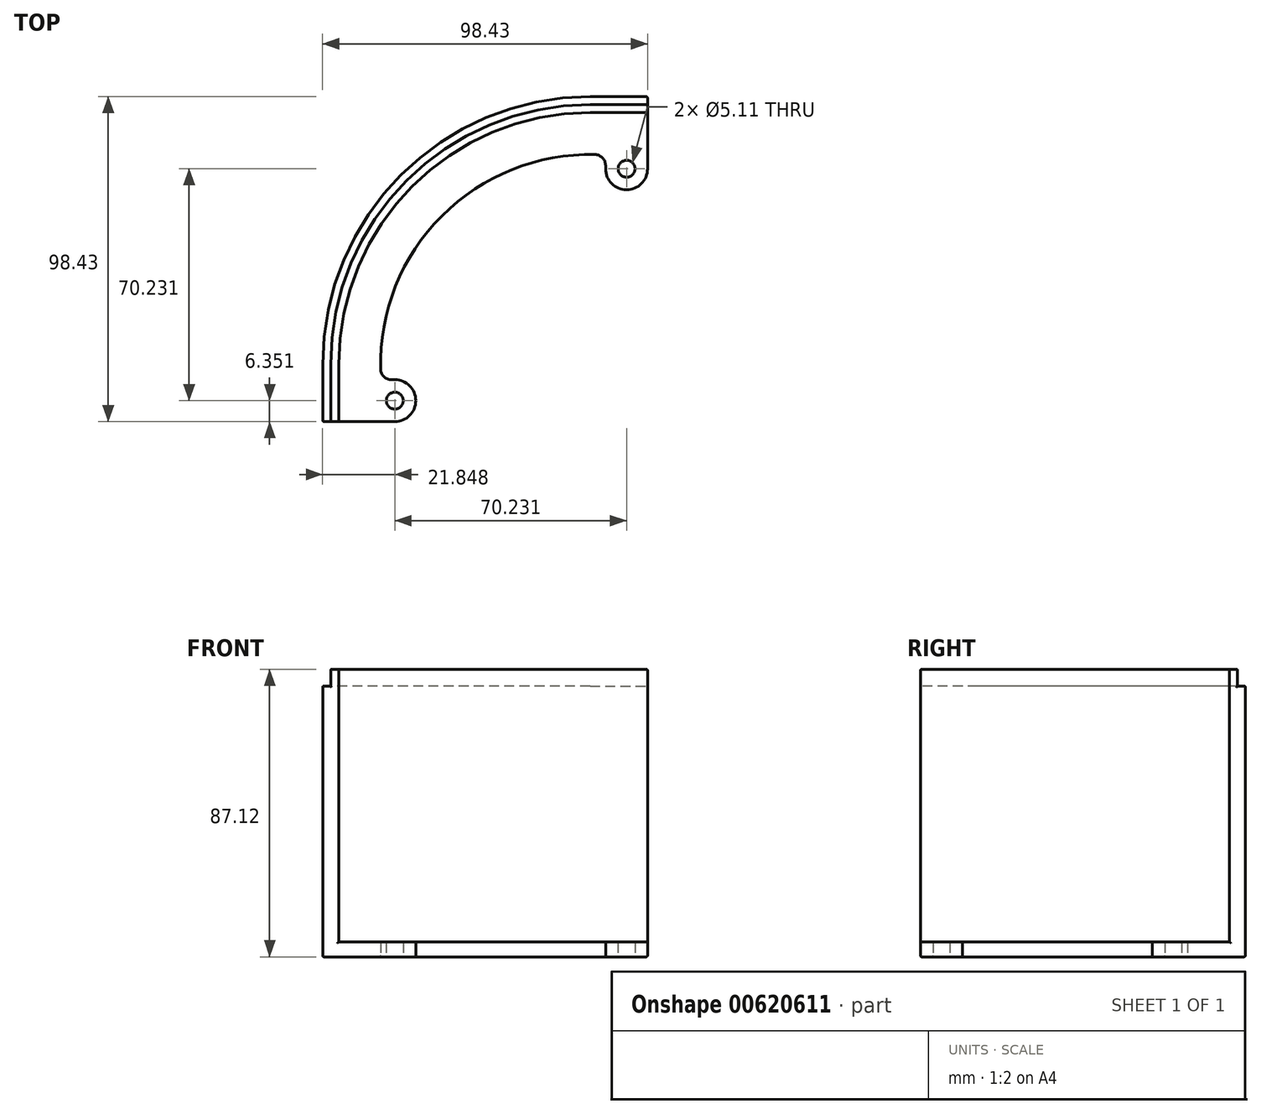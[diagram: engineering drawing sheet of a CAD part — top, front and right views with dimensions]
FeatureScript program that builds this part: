
annotation { "Feature Type Name" : "Feature", "Feature Type Description" : "" }
export const myFeature = defineFeature(function(context is Context, id is Id, definition is map)
    precondition{}
    {
        {
            var Q0;
            Q0=qCreatedBy(makeId("Top.planeOp"),FACE);
            var sketch = newSketch(context, id + "F0", { "sketchPlane" : qUnion([Q0])});
            skArc(sketch, "E0", {"start": v(1.47, 63.48) * mm, "mid": v(-44.9, 44.9) * mm, "end": v(-63.48, -1.47) * mm});
            skArc(sketch, "E1", {"start": v(0, 81.03) * mm, "mid": v(-57.3, 57.3) * mm, "end": v(-81.03, 0) * mm});
            skLineSegment(sketch, "E2", {"start": v(-81.03, 0) * mm, "end": v(-81.03, -17.4) * mm});
            skLineSegment(sketch, "E3", {"start": v(0, 81.03) * mm, "end": v(17.4, 81.03) * mm});
            skLineSegment(sketch, "E4", {"start": v(-81.03, -17.4) * mm, "end": v(-59.18, -17.4) * mm});
            skLineSegment(sketch, "E5", {"start": v(17.4, 81.03) * mm, "end": v(17.4, 59.18) * mm});
            skLineSegment(sketch, "E6", {"start": v(-60.18, -4.7) * mm, "end": v(-59.18, -4.7) * mm});
            skPoint(sketch, "E7.start.orphan", {"position": v(-63.5, 0) * mm});
            skArc(sketch, "E8", {"start": v(-59.18, -17.4) * mm, "mid": v(-52.83, -11.05) * mm, "end": v(-59.18, -4.7) * mm});
            skLineSegment(sketch, "E9.0", {"start": v(4.7, 60.18) * mm, "end": v(4.7, 59.18) * mm});
            skArc(sketch, "E10", {"start": v(4.7, 59.18) * mm, "mid": v(11.05, 52.83) * mm, "end": v(17.4, 59.18) * mm});
            skCircle(sketch, "E11", {"center": v(11.05, 59.18) * mm, "radius": 2.55 * mm});
            skCircle(sketch, "E12", {"center": v(-59.18, -11.05) * mm, "radius": 2.55 * mm});
            skPoint(sketch, "E13.visualSharp", {"position": v(4.7, 63.33) * mm});
            skArc(sketch, "E13.filletArc", {"start": v(4.7, 60.18) * mm, "mid": v(3.76, 62.49) * mm, "end": v(1.47, 63.48) * mm});
            skPoint(sketch, "E14.visualSharp", {"position": v(-63.33, -4.7) * mm});
            skArc(sketch, "E14.filletArc", {"start": v(-63.48, -1.47) * mm, "mid": v(-62.49, -3.76) * mm, "end": v(-60.18, -4.7) * mm});
            skArc(sketch, "E15", {"start": v(0, 78.61) * mm, "mid": v(-55.59, 55.59) * mm, "end": v(-78.61, 0) * mm});
            skLineSegment(sketch, "E16", {"start": v(0, 78.61) * mm, "end": v(17.4, 78.61) * mm});
            skLineSegment(sketch, "E17", {"start": v(-78.61, 0) * mm, "end": v(-78.61, -17.4) * mm});
            skArc(sketch, "E18", {"start": v(0, 76.2) * mm, "mid": v(-53.88, 53.88) * mm, "end": v(-76.2, 0) * mm});
            skLineSegment(sketch, "E19", {"start": v(0, 76.2) * mm, "end": v(17.4, 76.2) * mm});
            skLineSegment(sketch, "E20", {"start": v(-76.2, 0) * mm, "end": v(-76.2, -17.4) * mm});
            skSolve(sketch);
        }
        {
            var Q0;
            Q0=makeQuery(id+"F0.imprint","IMPRINT",FACE,{"disambiguationData":[TD([[makeQuery(id+"F0.imprint","IMPRINT",EDGE,{"derivedFrom":sQuery(id+"F0.wireOp",EDGE,"E0")}),-1.0]])]});
            extrude(context, id + "F1", {"entities" : qUnion([Q0]), "depth" : 4.57 * mm, "offsetDistance" : 25.4 * mm});
        }
        {
            var Q0;
            Q0=makeQuery(id+"F0.imprint","IMPRINT",FACE,{"disambiguationData":[TD([[makeQuery(id+"F0.imprint","IMPRINT",EDGE,{"derivedFrom":sQuery(id+"F0.wireOp",EDGE,"E15")}),1.0]])]});
            extrude(context, id + "F2", {"entities" : qUnion([Q0]), "operationType" : NewBodyOperationType.ADD, "depth" : 87.12 * mm, "offsetDistance" : 25.4 * mm});
        }
        {
            var Q0;
            Q0=makeQuery(id+"F0.imprint","IMPRINT",FACE,{"disambiguationData":[TD([[makeQuery(id+"F0.imprint","IMPRINT",EDGE,{"derivedFrom":sQuery(id+"F0.wireOp",EDGE,"E1")}),1.0]])]});
            extrude(context, id + "F3", {"entities" : qUnion([Q0]), "operationType" : NewBodyOperationType.ADD, "depth" : 82.04 * mm, "offsetDistance" : 25.4 * mm});
        }
        {
            var Q0;
            Q0=makeQuery(id+"F1.opExtrude","CAP_EDGE",EDGE,{"disambiguationData":[OSD([sQuery(id+"F0.wireOp",EDGE,"E4")])],"isStart":false});
            var Q1;
            Q1=makeQuery(id+"F1.opExtrude","CAP_EDGE",EDGE,{"disambiguationData":[OSD([sQuery(id+"F0.wireOp",EDGE,"E8")])],"isStart":false});
            var Q2;
            Q2=makeQuery(id+"F1.opExtrude","CAP_EDGE",EDGE,{"disambiguationData":[OSD([sQuery(id+"F0.wireOp",EDGE,"E14.filletArc")])],"isStart":false});
            var Q3;
            Q3=makeQuery(id+"F1.opExtrude","CAP_EDGE",EDGE,{"disambiguationData":[OSD([sQuery(id+"F0.wireOp",EDGE,"E0")])],"isStart":false});
            var Q4;
            {var subQ0=sQuery(id+"F0.wireOp",EDGE,"E5");Q4=makeQuery(id+"F3.boolean.opBoolean","MERGE",EDGE,{"derivedFrom":[makeQuery(id+"F2.boolean.opBoolean","MERGE",EDGE,{"derivedFrom":[makeQuery(id+"F1.opExtrude","CAP_EDGE",EDGE,{"disambiguationData":[OSD([subQ0])],"isStart":true}),makeQuery(id+"F2.opExtrude","CAP_EDGE",EDGE,{"disambiguationData":[OSD([subQ0])],"isStart":true})]}),makeQuery(id+"F3.opExtrude","CAP_EDGE",EDGE,{"disambiguationData":[OSD([subQ0])],"isStart":true})]});}
            var Q5;
            Q5=makeQuery(id+"F3.opExtrude","SWEPT_EDGE",EDGE,{"disambiguationData":[OSD([sQuery(id+"F0.wireOp",EDGE,"E3"),sQuery(id+"F0.wireOp",EDGE,"E5")])]});
            var Q6;
            Q6=makeQuery(id+"F2.opExtrude","SWEPT_EDGE",EDGE,{"disambiguationData":[OSD([sQuery(id+"F0.wireOp",EDGE,"E5"),sQuery(id+"F0.wireOp",EDGE,"E19")])]});
            var Q7;
            Q7=makeQuery(id+"F2.opExtrude","SWEPT_EDGE",EDGE,{"disambiguationData":[OSD([sQuery(id+"F0.wireOp",EDGE,"E4"),sQuery(id+"F0.wireOp",EDGE,"E20")])]});
            var Q8;
            Q8=makeQuery(id+"F3.opExtrude","SWEPT_EDGE",EDGE,{"disambiguationData":[OSD([sQuery(id+"F0.wireOp",EDGE,"E2"),sQuery(id+"F0.wireOp",EDGE,"E4")])]});
            var Q9;
            Q9=makeQuery(id+"F3.opExtrude","CAP_EDGE",EDGE,{"disambiguationData":[OSD([sQuery(id+"F0.wireOp",EDGE,"E17")])],"isStart":false});
            var Q10;
            Q10=makeQuery(id+"F3.opExtrude","CAP_EDGE",EDGE,{"disambiguationData":[OSD([sQuery(id+"F0.wireOp",EDGE,"E1")])],"isStart":false});
            var Q11;
            Q11=makeQuery(id+"F3.opExtrude","CAP_EDGE",EDGE,{"disambiguationData":[OSD([sQuery(id+"F0.wireOp",EDGE,"E4")])],"isStart":false});
            var Q12;
            Q12=makeQuery(id+"F3.opExtrude","CAP_EDGE",EDGE,{"disambiguationData":[OSD([sQuery(id+"F0.wireOp",EDGE,"E5")])],"isStart":false});
            var Q13;
            Q13=makeQuery(id+"F3.opExtrude","CAP_EDGE",EDGE,{"disambiguationData":[OSD([sQuery(id+"F0.wireOp",EDGE,"E1")])],"isStart":true});
            var Q14;
            Q14=makeQuery(id+"F1.opExtrude","CAP_EDGE",EDGE,{"disambiguationData":[OSD([sQuery(id+"F0.wireOp",EDGE,"E11")])],"isStart":true});
            var Q15;
            Q15=makeQuery(id+"F1.opExtrude","CAP_EDGE",EDGE,{"disambiguationData":[OSD([sQuery(id+"F0.wireOp",EDGE,"E12")])],"isStart":true});
            var Q16;
            Q16=makeQuery(id+"F1.opExtrude","CAP_EDGE",EDGE,{"disambiguationData":[OSD([sQuery(id+"F0.wireOp",EDGE,"E11")])],"isStart":false});
            var Q17;
            Q17=makeQuery(id+"F1.opExtrude","CAP_EDGE",EDGE,{"disambiguationData":[OSD([sQuery(id+"F0.wireOp",EDGE,"E12")])],"isStart":false});
            var Q18;
            Q18=makeQuery(id+"F3.opExtrude","SWEPT_EDGE",EDGE,{"disambiguationData":[OSD([sQuery(id+"F0.wireOp",EDGE,"E4"),sQuery(id+"F0.wireOp",EDGE,"E17")])]});
            var Q19;
            Q19=makeQuery(id+"F2.opExtrude","CAP_EDGE",EDGE,{"disambiguationData":[OSD([sQuery(id+"F0.wireOp",EDGE,"E4")])],"isStart":false});
            var Q20;
            Q20=makeQuery(id+"F2.opExtrude","CAP_EDGE",EDGE,{"disambiguationData":[OSD([sQuery(id+"F0.wireOp",EDGE,"E5")])],"isStart":false});
            var Q21;
            Q21=makeQuery(id+"F3.opExtrude","SWEPT_EDGE",EDGE,{"disambiguationData":[OSD([sQuery(id+"F0.wireOp",EDGE,"E5"),sQuery(id+"F0.wireOp",EDGE,"E16")])]});
            var Q22;
            Q22=makeQuery(id+"F2.opExtrude","CAP_EDGE",EDGE,{"disambiguationData":[OSD([sQuery(id+"F0.wireOp",EDGE,"E20")])],"isStart":false});
            fillet(context, id + "F4", {"entities" : qUnion([Q0, Q1, Q2, Q3, Q4, Q5, Q6, Q7, Q8, Q9, Q10, Q11, Q12, Q13, Q14, Q15, Q16, Q17, Q18, Q19, Q20, Q21, Q22]), "radius" : 0.38 * mm, "tangentPropagation" : true, "allowEdgeOverflow" : false});
        }
        {
            var Q0;
            Q0=makeQuery(id+"F2.opExtrude","CAP_EDGE",EDGE,{"disambiguationData":[OSD([sQuery(id+"F0.wireOp",EDGE,"E15")])],"isStart":false});
            var Q1;
            Q1=makeQuery(id+"F2.opExtrude","CAP_EDGE",EDGE,{"disambiguationData":[OSD([sQuery(id+"F0.wireOp",EDGE,"E16")])],"isStart":false});
            var Q2;
            Q2=makeQuery(id+"F1.opExtrude","CAP_EDGE",EDGE,{"disambiguationData":[OSD([sQuery(id+"F0.wireOp",EDGE,"E18")])],"isStart":false});
            fillet(context, id + "F5", {"entities" : qUnion([Q0, Q1, Q2]), "radius" : 0.25 * mm, "tangentPropagation" : true, "allowEdgeOverflow" : false});
        }
    });
